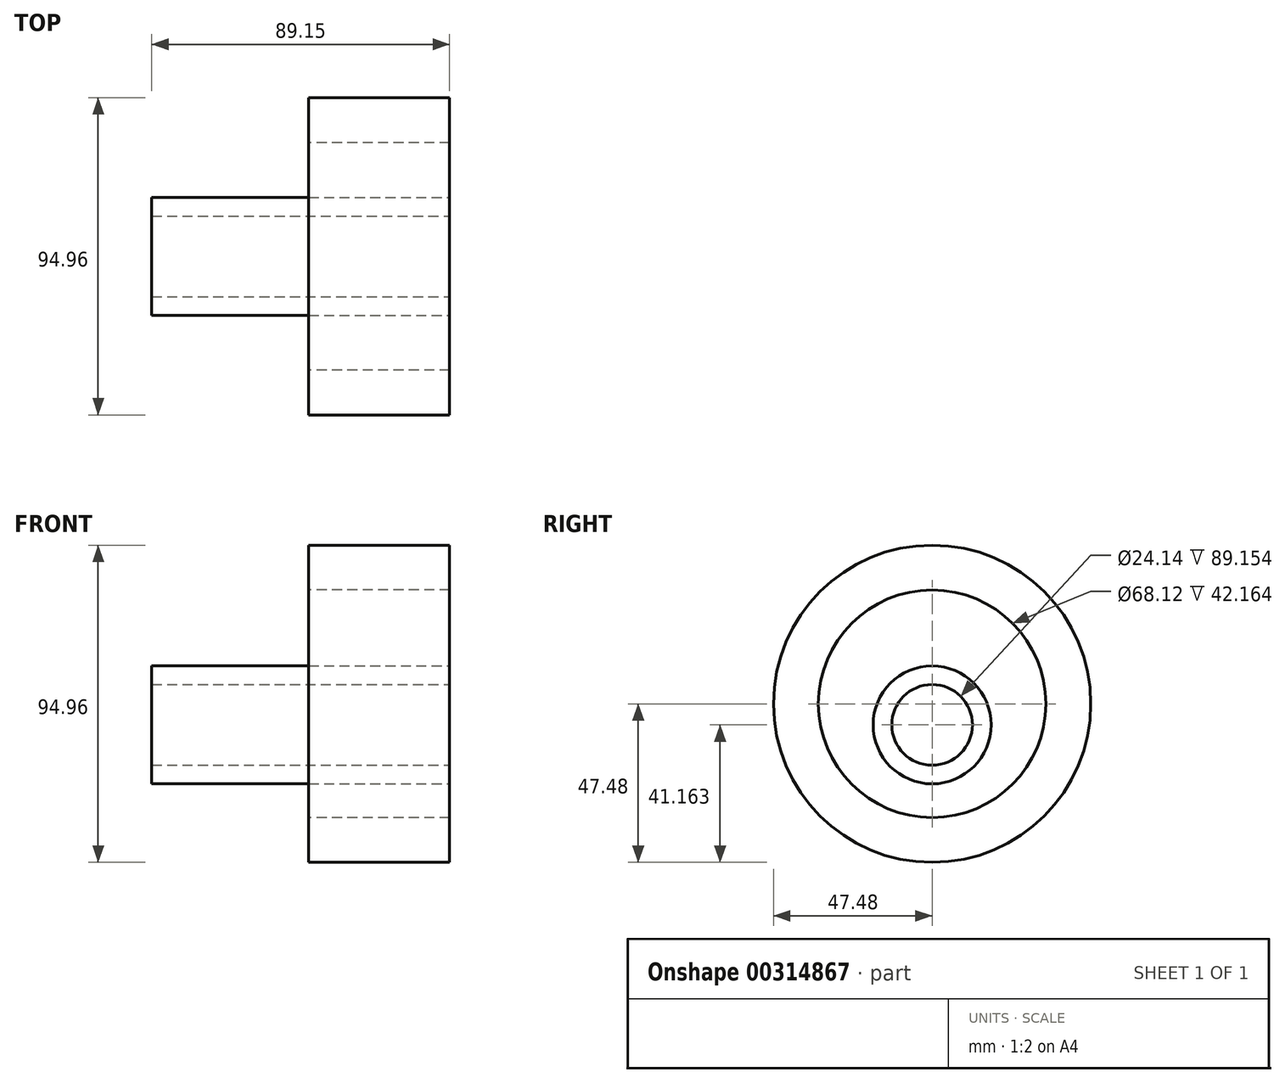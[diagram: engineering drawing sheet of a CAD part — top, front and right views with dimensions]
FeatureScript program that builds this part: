
annotation { "Feature Type Name" : "Feature", "Feature Type Description" : "" }
export const myFeature = defineFeature(function(context is Context, id is Id, definition is map)
    precondition{}
    {
        {
            var Q0;
            Q0=qCreatedBy(makeId("Right.planeOp"),FACE);
            var sketch = newSketch(context, id + "F0", { "sketchPlane" : qUnion([Q0])});
            skCircle(sketch, "E0", {"center": v(0, 0) * mm, "radius": 47.48 * mm});
            skCircle(sketch, "E1", {"center": v(0, 0) * mm, "radius": 34.06 * mm});
            skSolve(sketch);
        }
        {
            var Q0;
            Q0=makeQuery(id+"F0.imprint","IMPRINT",FACE,{"disambiguationData":[TD([[makeQuery(id+"F0.imprint","IMPRINT",EDGE,{"derivedFrom":sQuery(id+"F0.wireOp",EDGE,"E0")}),1.0]])]});
            extrude(context, id + "F1", {"entities" : qUnion([Q0]), "depth" : 16.76 * mm});
        }
        {
            var Q0;
            Q0=makeQuery(id+"F1.opExtrude","CAP_FACE",FACE,{"disambiguationData":[OSD([sQuery(id+"F0.wireOp",EDGE,"E0"),sQuery(id+"F0.wireOp",EDGE,"E1")])],"isStart":false});
            extrude(context, id + "F2", {"entities" : qUnion([Q0]), "operationType" : NewBodyOperationType.ADD, "depth" : 25.4 * mm});
        }
        {
            var Q0;
            Q0=makeQuery(id+"F2.opExtrude","CAP_FACE",FACE,{"disambiguationData":[OSD([sQuery(id+"F0.wireOp",EDGE,"E0"),sQuery(id+"F0.wireOp",EDGE,"E1")])],"isStart":false});
            var sketch = newSketch(context, id + "F3", { "sketchPlane" : qUnion([Q0])});
            skCircle(sketch, "E2", {"center": v(0, -6.32) * mm, "radius": 12.07 * mm});
            skCircle(sketch, "E3", {"center": v(0, -6.32) * mm, "radius": 17.65 * mm});
            skSolve(sketch);
        }
        {
            var Q0;
            Q0 = qSketchRegion(id + "F3", true);
            extrude(context, id + "F4", {"entities" : qUnion([Q0]), "oppositeDirection" : true, "depth" : 89.15 * mm});
        }
    });
